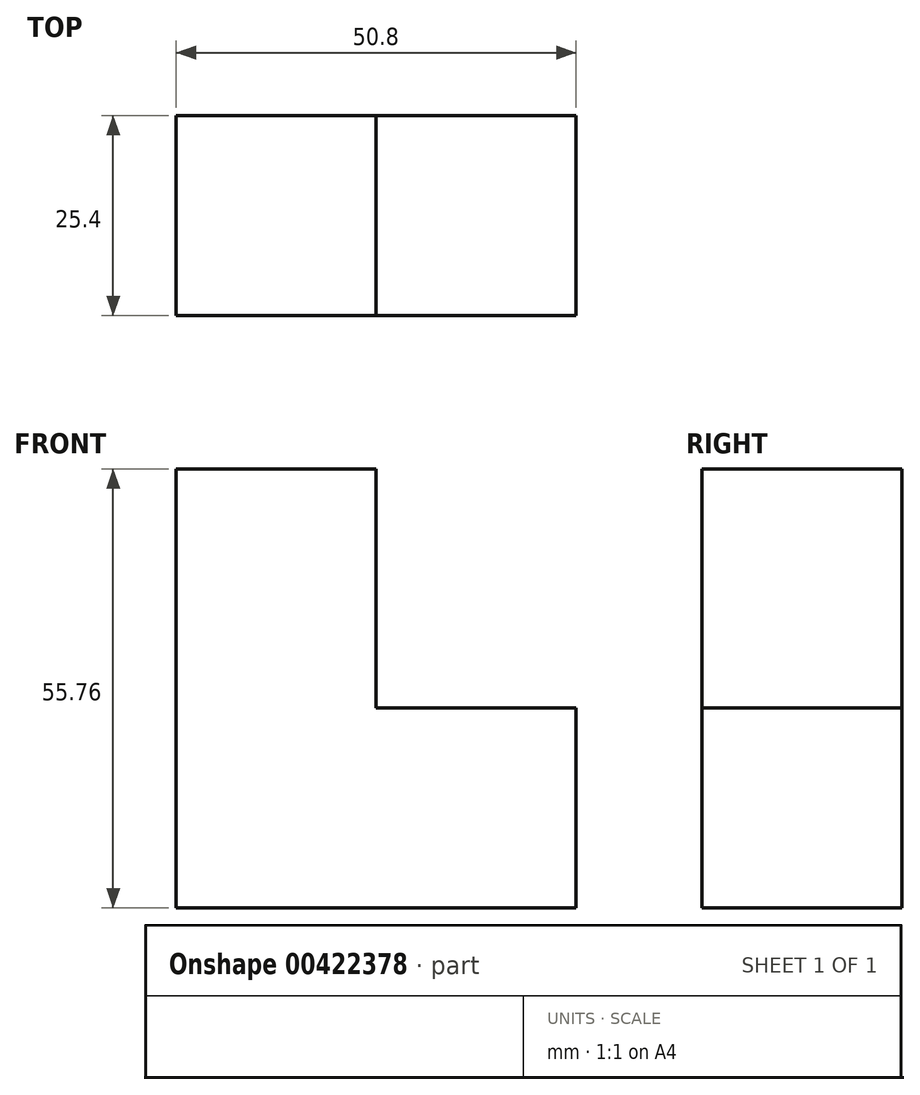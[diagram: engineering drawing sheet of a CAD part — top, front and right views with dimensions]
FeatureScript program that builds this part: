
annotation { "Feature Type Name" : "Feature", "Feature Type Description" : "" }
export const myFeature = defineFeature(function(context is Context, id is Id, definition is map)
    precondition{}
    {
        {
            var Q0;
            Q0=qCreatedBy(makeId("Front.planeOp"),FACE);
            var sketch = newSketch(context, id + "F0", { "sketchPlane" : qUnion([Q0])});
            skLineSegment(sketch, "E0", {"start": v(-62.82, 55.76) * mm, "end": v(-62.82, 0) * mm});
            skLineSegment(sketch, "E1", {"start": v(-62.82, 0) * mm, "end": v(-12.02, 0) * mm});
            skLineSegment(sketch, "E2", {"start": v(-12.02, 0) * mm, "end": v(-12.02, 25.4) * mm});
            skLineSegment(sketch, "E3", {"start": v(-12.02, 25.4) * mm, "end": v(-37.42, 25.4) * mm});
            skLineSegment(sketch, "E4", {"start": v(-37.42, 25.4) * mm, "end": v(-37.42, 50.8) * mm});
            skLineSegment(sketch, "E5", {"start": v(-37.42, 50.8) * mm, "end": v(-37.42, 55.76) * mm});
            skLineSegment(sketch, "E6", {"start": v(-37.42, 55.76) * mm, "end": v(-62.82, 55.76) * mm});
            skSolve(sketch);
        }
        {
            var Q0;
            Q0=makeQuery(id+"F0.imprint","IMPRINT",FACE,{"disambiguationData":[TD([[makeQuery(id+"F0.imprint","IMPRINT",EDGE,{"derivedFrom":sQuery(id+"F0.wireOp",EDGE,"E0")}),1.0]])]});
            extrude(context, id + "F1", {"entities" : qUnion([Q0]), "depth" : 25.4 * mm});
        }
    });
